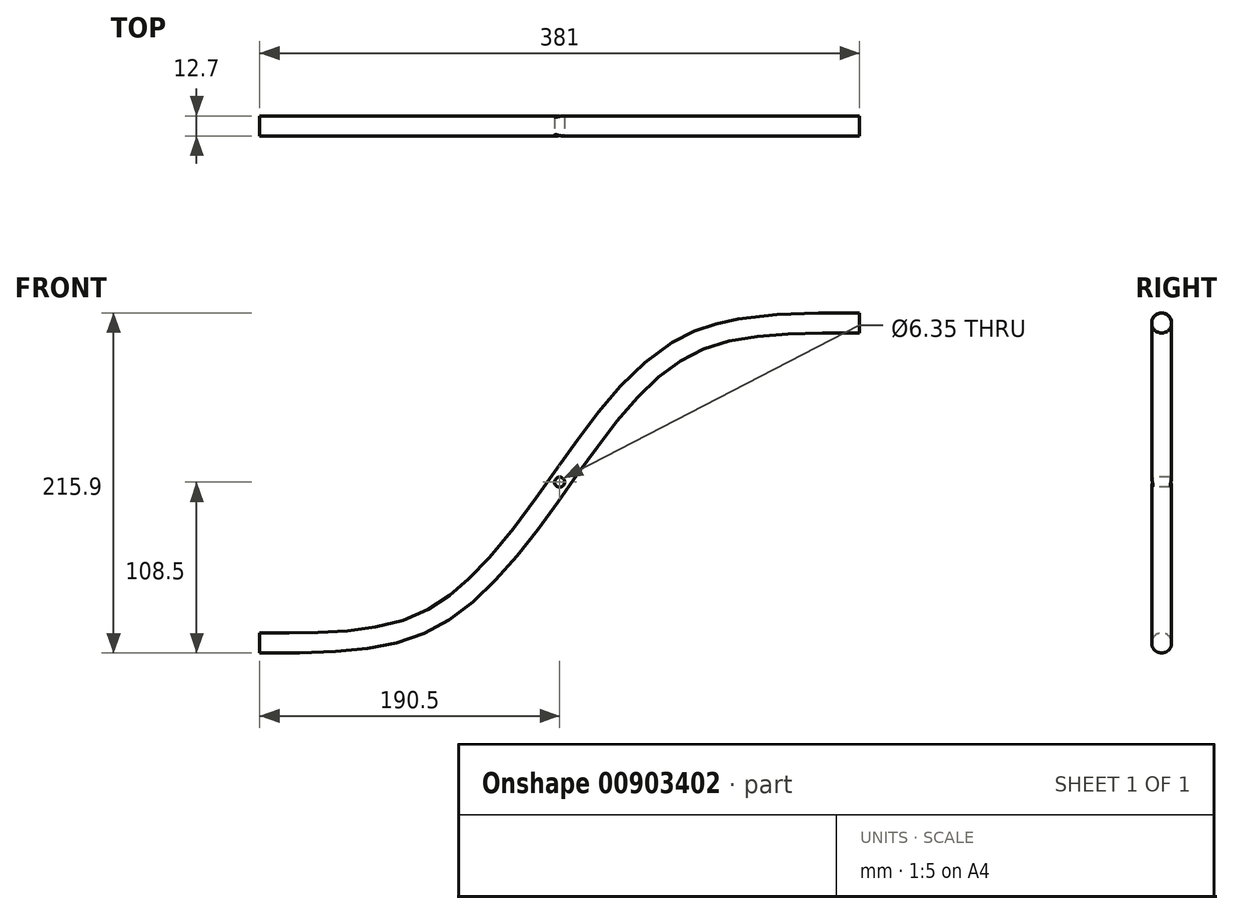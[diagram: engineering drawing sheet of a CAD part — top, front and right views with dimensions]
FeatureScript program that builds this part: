
annotation { "Feature Type Name" : "Feature", "Feature Type Description" : "" }
export const myFeature = defineFeature(function(context is Context, id is Id, definition is map)
    precondition{}
    {
        {
            var Q0;
            Q0=qCreatedBy(makeId("Front.planeOp"),FACE);
            var sketch = newSketch(context, id + "F0", { "sketchPlane" : qUnion([Q0])});
            skFitSpline(sketch, "E0", {"points": [v(0, 0) * mm, v(113.2, 17.6) * mm, v(190.5, 102.15) * mm, v(267.61, 186.87) * mm, v(381, 203.2) * mm], "startDerivative": vector(621.45, 0) * mm, "endDerivative": vector(569.13, 0) * mm});
            skLineSegment(sketch, "E1", {"start": v(0, 0) * mm, "end": v(113.2, 17.6) * mm, "construction": true});
            skLineSegment(sketch, "E2", {"start": v(113.2, 17.6) * mm, "end": v(190.5, 102.15) * mm, "construction": true});
            skLineSegment(sketch, "E3", {"start": v(190.5, 102.15) * mm, "end": v(267.61, 186.87) * mm, "construction": true});
            skLineSegment(sketch, "E4", {"start": v(267.61, 186.87) * mm, "end": v(381, 203.2) * mm, "construction": true});
            skCircle(sketch, "E5", {"center": v(190.5, 102.15) * mm, "radius": 3.18 * mm});
            skSolve(sketch);
        }
        {
            var Q0;
            Q0=qCreatedBy(makeId("Right.planeOp"),FACE);
            var sketch = newSketch(context, id + "F1", { "sketchPlane" : qUnion([Q0])});
            skCircle(sketch, "E6", {"center": v(0, 0) * mm, "radius": 6.35 * mm});
            skSolve(sketch);
        }
        {
            var Q0;
            Q0=makeQuery(id+"F1.imprint","IMPRINT",FACE,{"disambiguationData":[TD([[makeQuery(id+"F1.imprint","IMPRINT",EDGE,{"derivedFrom":sQuery(id+"F1.wireOp",EDGE,"E6")}),1.0]])]});
            var Q1;
            Q1=sQuery(id+"F0.wireOp",EDGE,"E0");
            sweep(context, id + "F2", {"profiles" : qUnion([Q0]), "path" : qUnion([Q1])});
        }
        {
            var Q0;
            Q0 = qSketchRegion(id + "F0", true);
            extrude(context, id + "F3", {"entities" : qUnion([Q0]), "operationType" : NewBodyOperationType.REMOVE, "endBound" : BoundingType.SYMMETRIC, "oppositeDirection" : true, "depth" : 25.4 * mm, "offsetDistance" : 25.4 * mm});
        }
    });
